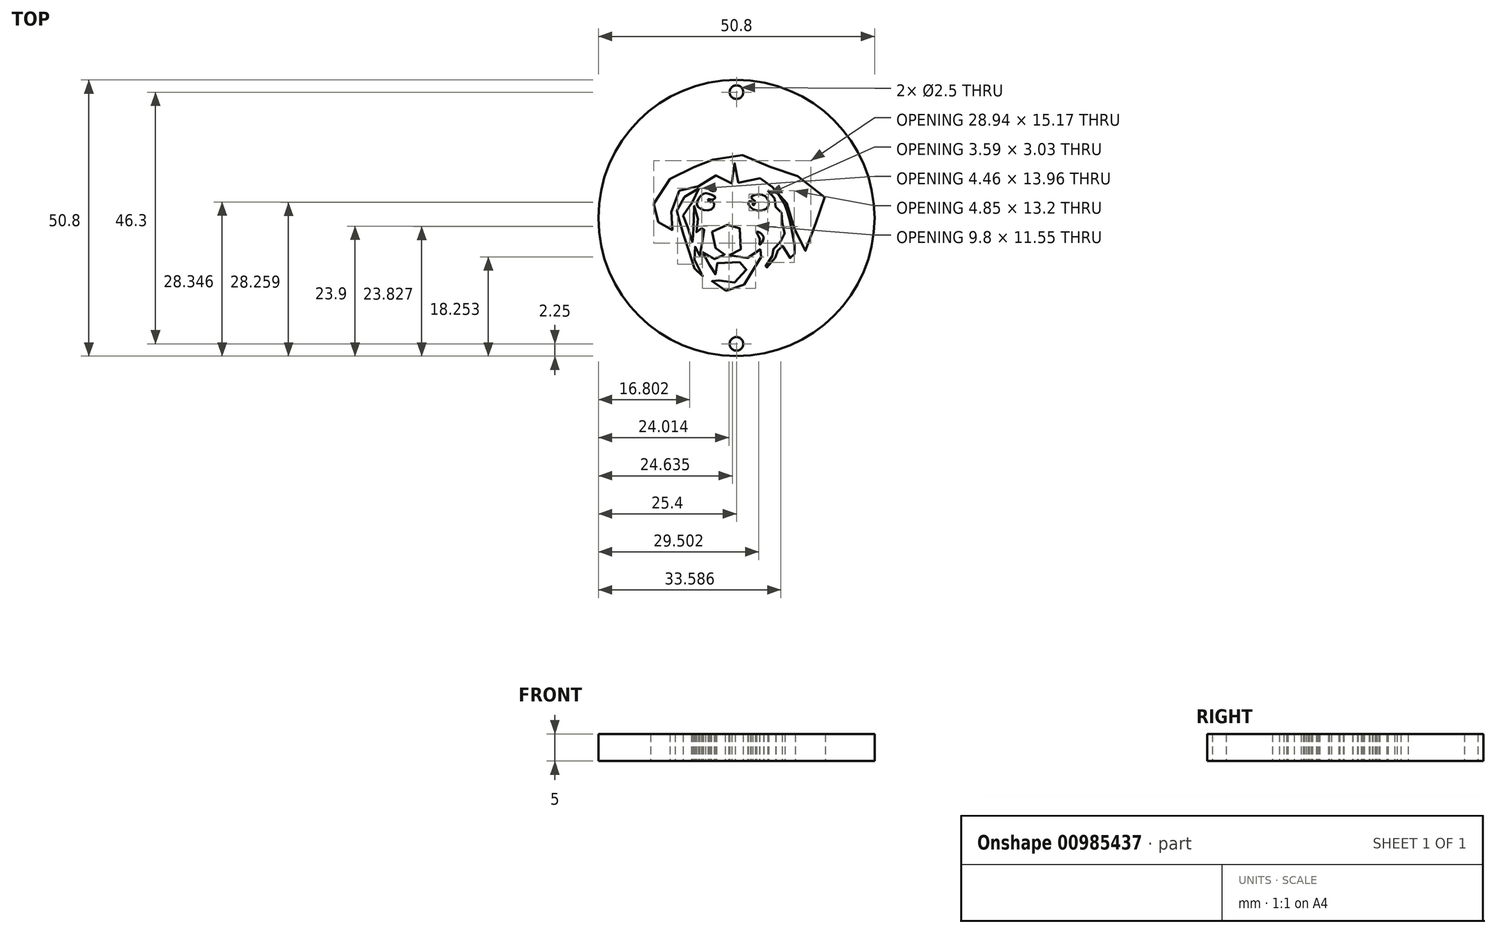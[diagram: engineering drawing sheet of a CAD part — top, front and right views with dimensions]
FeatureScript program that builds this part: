
annotation { "Feature Type Name" : "Feature", "Feature Type Description" : "" }
export const myFeature = defineFeature(function(context is Context, id is Id, definition is map)
    precondition{}
    {
        {
            var Q0;
            Q0=qCreatedBy(makeId("Top.planeOp"),FACE);
            var sketch = newSketch(context, id + "F0", { "sketchPlane" : qUnion([Q0])});
            skCircle(sketch, "E0", {"center": v(0, 0) * mm, "radius": 25.4 * mm});
            skCircle(sketch, "E1", {"center": v(0, 23.15) * mm, "radius": 1.25 * mm});
            skCircle(sketch, "E2", {"center": v(0, -23.15) * mm, "radius": 1.25 * mm});
            skFitSpline(sketch, "E3", {"points": [v(-15.23, 2.6) * mm, v(-12.94, 6.83) * mm, v(-11.8, 7.4) * mm, v(-8.77, 9.55) * mm, v(-7.25, 9.11) * mm, v(-6.39, 9.84) * mm, v(-3.16, 11.05) * mm, v(0, 11.6) * mm, v(3.71, 10.87) * mm, v(6.52, 9.3) * mm, v(9.46, 8.94) * mm, v(13.7, 5.61) * mm, v(16.3, 3.53) * mm, v(15.26, 0) * mm, v(14.25, -1.83) * mm, v(13.04, -5.93) * mm, v(11.23, -4.99) * mm, v(10.72, -2.29) * mm, v(10.02, 1.08) * mm, v(9.12, 2.97) * mm, v(8.25, 4.67) * mm, v(6.49, 5.74) * mm, v(5.26, 5.5) * mm, v(4.88, 6.79) * mm, v(3.3, 7.6) * mm, v(1.28, 7.17) * mm, v(0, 6.38) * mm, v(-0.22, 8.64) * mm, v(-0.51, 10.2) * mm, v(-1.4, 9.48) * mm, v(-0.9, 6.23) * mm, v(-2.32, 7.22) * mm, v(-3.4, 7.86) * mm, v(-5.01, 7.24) * mm, v(-6.01, 6.24) * mm, v(-7.99, 5.74) * mm, v(-9.5, 5.58) * mm, v(-10.51, 4.96) * mm, v(-10.7, 3.79) * mm, v(-11.85, 1.4) * mm, v(-12.12, 0) * mm, v(-11.3, -1.2) * mm, v(-12.92, -2.88) * mm, v(-14.09, -2) * mm, v(-14.67, 0) * mm, v(-15.76, 1.76) * mm, v(-15.23, 2.6) * mm]});
            skFitSpline(sketch, "E4", {"points": [v(-6.29, -6.26) * mm, v(-4.94, -7.68) * mm, v(-3.92, -7.49) * mm, v(-2.44, -7.23) * mm, v(-2.11, -6.72) * mm, v(-2.54, -6.82) * mm, v(-3.05, -6.55) * mm, v(-4.07, -5.12) * mm, v(-4.72, -3.37) * mm, v(-3.63, -1.6) * mm, v(-1.75, -1.3) * mm, v(-0.9, -1.02) * mm, v(0.46, -1.74) * mm, v(1.24, -3.9) * mm, v(0, -6.7) * mm, v(-1.17, -6.62) * mm, v(-1.27, -7.13) * mm, v(1.26, -7.43) * mm, v(3.95, -6.7) * mm, v(4.42, -5.72) * mm, v(4.94, -5.3) * mm, v(4.6, -7.07) * mm, v(3.13, -9.35) * mm, v(2.56, -10.6) * mm, v(2.46, -11.53) * mm, v(0, -12.86) * mm, v(-1.78, -13.4) * mm, v(-3.75, -12.48) * mm, v(-4.59, -11.38) * mm, v(-4.49, -10.77) * mm, v(-3.41, -11.36) * mm, v(-1.77, -12.09) * mm, v(0, -11.7) * mm, v(1.29, -10.57) * mm, v(2.05, -8.53) * mm, v(1.82, -8.25) * mm, v(-0.8, -8.1) * mm, v(-3.67, -8.4) * mm, v(-3.91, -9.33) * mm, v(-3.69, -10.21) * mm, v(-4.81, -10.36) * mm, v(-4.8, -8.88) * mm, v(-5.88, -8.06) * mm, v(-6.29, -6.26) * mm]});
            skFitSpline(sketch, "E5", {"points": [v(3.74, -2.54) * mm, v(4.25, -3.78) * mm, v(4.29, -4.9) * mm, v(4.95, -3.45) * mm, v(3.74, -2.54) * mm]});
            skFitSpline(sketch, "E6", {"points": [v(5.76, 5.03) * mm, v(7.16, 3.33) * mm, v(7.24, 1.94) * mm, v(8.27, 0.98) * mm, v(8.4, -0.87) * mm, v(8.85, -3.36) * mm, v(7.43, -4.9) * mm, v(6.63, -6.26) * mm, v(6.38, -7.49) * mm, v(5.05, -9.37) * mm, v(6.52, -8.25) * mm, v(7.47, -6.26) * mm, v(7.62, -5.93) * mm, v(8.42, -5.13) * mm, v(9.03, -5.93) * mm, v(9.49, -6.73) * mm, v(10.14, -7.49) * mm, v(10.76, -6.26) * mm, v(10.67, -4.99) * mm, v(10.08, -1.77) * mm, v(9.4, 1.08) * mm, v(8.94, 1.96) * mm, v(8.1, 4.13) * mm, v(5.76, 5.03) * mm]});
            skFitSpline(sketch, "E7", {"points": [v(-4.3, 5.85) * mm, v(-4.95, 5.3) * mm, v(-3.92, 5.07) * mm, v(-4.3, 5.85) * mm]});
            skFitSpline(sketch, "E8", {"points": [v(-5.22, 3.48) * mm, v(-4.3, 3.4) * mm, v(-3.92, 3.87) * mm, v(-4.95, 4.41) * mm, v(-6.01, 4.5) * mm, v(-7.05, 3.37) * mm, v(-7.25, 2.26) * mm, v(-6.01, 1.48) * mm, v(-4.3, 1.86) * mm, v(-4.3, 2.97) * mm, v(-4.95, 2.97) * mm, v(-5.22, 3.48) * mm]});
            skFitSpline(sketch, "E9", {"points": [v(2.7, 3.7) * mm, v(3.55, 4.3) * mm, v(5.24, 4.05) * mm, v(5.9, 2.97) * mm, v(5.65, 1.86) * mm, v(3.2, 1.53) * mm, v(2.22, 2.97) * mm, v(2.93, 2.97) * mm, v(3.02, 2.36) * mm, v(3.45, 2.97) * mm, v(2.7, 3.7) * mm]});
            skFitSpline(sketch, "E10", {"points": [v(-6.92, 5.48) * mm, v(-8.82, 5.18) * mm, v(-9.49, 4.02) * mm, v(-9.95, 3.06) * mm, v(-10.55, 2.01) * mm, v(-11.15, 1) * mm, v(-11.25, 0.37) * mm, v(-11.05, -0.33) * mm, v(-10.55, -0.21) * mm, v(-10.19, -1.27) * mm, v(-9.89, -2.56) * mm, v(-9.5, -3.96) * mm, v(-9.04, -5.26) * mm, v(-8.54, -6.62) * mm, v(-8.2, -8.13) * mm, v(-7.5, -9.7) * mm, v(-6.29, -11.26) * mm, v(-6.1, -11) * mm, v(-6.52, -10.35) * mm, v(-7.26, -8.76) * mm, v(-7.9, -7.18) * mm, v(-8.2, -5.87) * mm, v(-7.79, -5.25) * mm, v(-7.26, -5.66) * mm, v(-7, -6.83) * mm, v(-6.81, -7.18) * mm, v(-6.74, -6.06) * mm, v(-6.62, -5.37) * mm, v(-6.3, -5.09) * mm, v(-6.38, -4.35) * mm, v(-6.36, -3.2) * mm, v(-6.1, -2.54) * mm, v(-5.79, -1.87) * mm, v(-5.7, -1.32) * mm, v(-6.1, -1.23) * mm, v(-6.4, -1.87) * mm, v(-6.83, -2.68) * mm, v(-7, -3.06) * mm, v(-7.33, -2.94) * mm, v(-7.33, -2.51) * mm, v(-7.45, -1.44) * mm, v(-7.05, -0.7) * mm, v(-7.1, 0) * mm, v(-7.14, 1.01) * mm, v(-7.45, 1.85) * mm, v(-7.86, 2.23) * mm, v(-7.98, 1.4) * mm, v(-7.79, 0.47) * mm, v(-8.03, -0.75) * mm, v(-8.29, -1.65) * mm, v(-7.93, -3.42) * mm, v(-7.72, -4.25) * mm, v(-7.57, -4.59) * mm, v(-7.86, -4.68) * mm, v(-8.29, -4.01) * mm, v(-8.74, -2.77) * mm, v(-8.96, -1.73) * mm, v(-9.5, -1.15) * mm, v(-9.77, -0.49) * mm, v(-9.81, 0.32) * mm, v(-9.46, 1.4) * mm, v(-8.26, 2.33) * mm, v(-8.07, 3.56) * mm, v(-7.84, 4.28) * mm, v(-6.92, 5.48) * mm]});
            skSolve(sketch);
        }
        {
            var Q0;
            Q0 = qSketchRegion(id + "F0", true);
            extrude(context, id + "F1", {"entities" : qUnion([Q0]), "depth" : 5 * mm, "offsetDistance" : 25 * mm});
        }
    });
